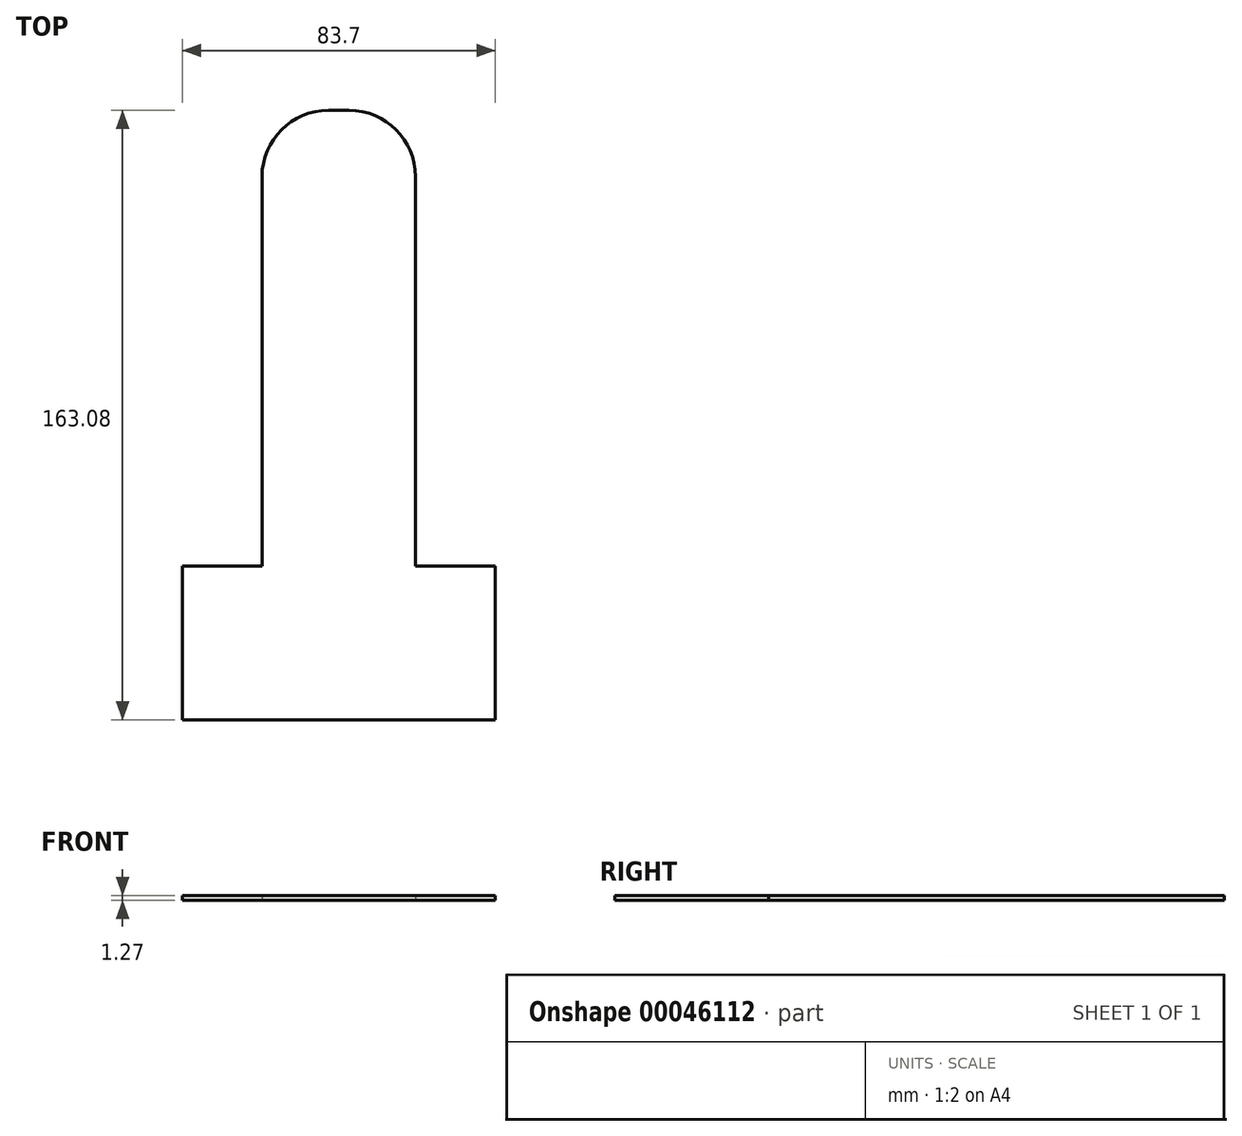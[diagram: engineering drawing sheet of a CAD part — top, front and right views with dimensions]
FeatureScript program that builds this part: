
annotation { "Feature Type Name" : "Feature", "Feature Type Description" : "" }
export const myFeature = defineFeature(function(context is Context, id is Id, definition is map)
    precondition{}
    {
        {
            var Q0;
            Q0=qCreatedBy(makeId("Top.planeOp"),FACE);
            var sketch = newSketch(context, id + "F0", { "sketchPlane" : qUnion([Q0])});
            skLineSegment(sketch, "E0", {"start": v(-41.85, -20.58) * mm, "end": v(41.85, -20.58) * mm});
            skLineSegment(sketch, "E1", {"start": v(-20.53, 142.5) * mm, "end": v(-20.53, 20.58) * mm});
            skLineSegment(sketch, "E2", {"start": v(-41.85, -20.58) * mm, "end": v(-41.85, 20.58) * mm});
            skLineSegment(sketch, "E3", {"start": v(41.85, 20.58) * mm, "end": v(41.85, -20.58) * mm});
            skLineSegment(sketch, "E4", {"start": v(-20.53, 20.58) * mm, "end": v(-41.85, 20.58) * mm});
            skLineSegment(sketch, "E5.MirrorCS", {"start": v(20.53, 142.5) * mm, "end": v(20.53, 20.58) * mm});
            skLineSegment(sketch, "E6", {"start": v(-20.53, 142.5) * mm, "end": v(20.53, 142.5) * mm});
            skLineSegment(sketch, "E7", {"start": v(20.53, 20.58) * mm, "end": v(41.85, 20.58) * mm});
            skSolve(sketch);
        }
        {
            var Q0;
            Q0 = qSketchRegion(id + "F0", true);
            extrude(context, id + "F1", {"entities" : qUnion([Q0]), "depth" : 1.27 * mm});
        }
        {
            var Q0;
            Q0=makeQuery(id+"F1.opExtrude","SWEPT_EDGE",EDGE,{"disambiguationData":[OSD([sQuery(id+"F0.wireOp",EDGE,"E1"),sQuery(id+"F0.wireOp",EDGE,"E6")])]});
            var Q1;
            Q1=makeQuery(id+"F1.opExtrude","SWEPT_EDGE",EDGE,{"disambiguationData":[OSD([sQuery(id+"F0.wireOp",EDGE,"E5.MirrorCS"),sQuery(id+"F0.wireOp",EDGE,"E6")])]});
            fillet(context, id + "F2", {"entities" : qUnion([Q0, Q1]), "radius" : 17.78 * mm, "tangentPropagation" : true, "allowEdgeOverflow" : false});
        }
    });
